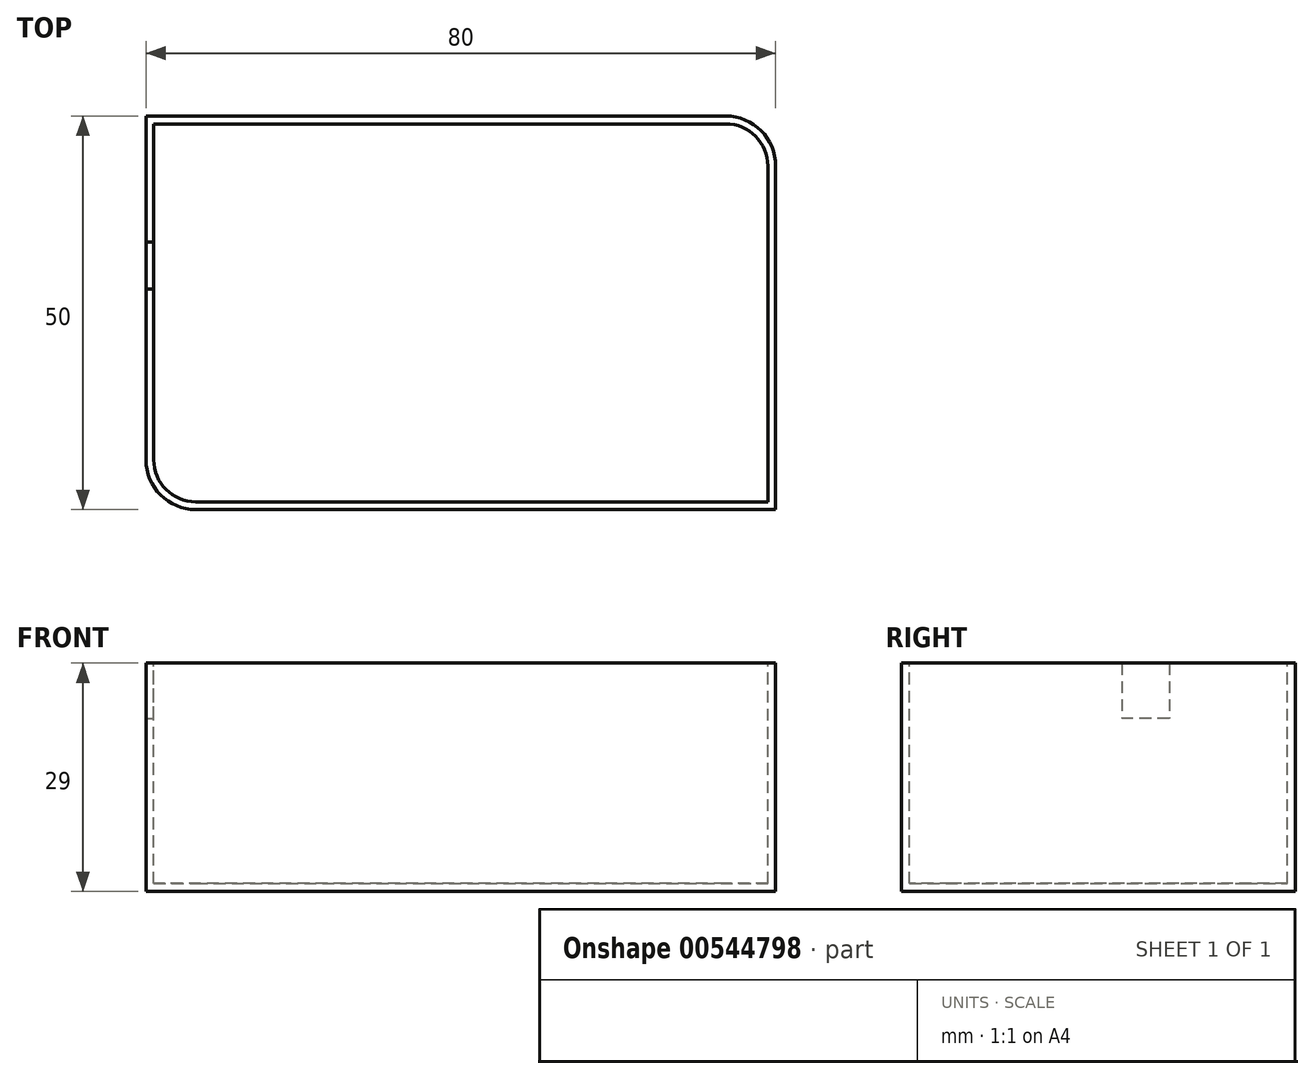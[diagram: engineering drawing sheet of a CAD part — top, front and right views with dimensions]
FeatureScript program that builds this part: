
annotation { "Feature Type Name" : "Feature", "Feature Type Description" : "" }
export const myFeature = defineFeature(function(context is Context, id is Id, definition is map)
    precondition{}
    {
        {
            var Q0;
            Q0=qCreatedBy(makeId("Top.planeOp"),FACE);
            var sketch = newSketch(context, id + "F0", { "sketchPlane" : qUnion([Q0])});
            skLineSegment(sketch, "E0.bottom", {"start": v(40, -25) * mm, "end": v(-33.65, -25) * mm});
            skLineSegment(sketch, "E0.top", {"start": v(33.65, 25) * mm, "end": v(-40, 25) * mm});
            skLineSegment(sketch, "E0.left", {"start": v(40, -25) * mm, "end": v(40, 18.65) * mm});
            skLineSegment(sketch, "E0.right", {"start": v(-40, -18.65) * mm, "end": v(-40, 25) * mm});
            skPoint(sketch, "E0.middle", {"position": v(0, 0) * mm});
            skPoint(sketch, "E1.visualSharp", {"position": v(-40, 25) * mm});
            skLineSegment(sketch, "E1.filletArc", {"start": v(-40, 25) * mm, "end": v(-40, 25) * mm});
            skPoint(sketch, "E2.visualSharp", {"position": v(40, -25) * mm});
            skLineSegment(sketch, "E2.filletArc", {"start": v(40, -25) * mm, "end": v(40, -25) * mm});
            skPoint(sketch, "E3.visualSharp", {"position": v(-40, -25) * mm});
            skArc(sketch, "E3.filletArc", {"start": v(-40, -18.65) * mm, "mid": v(-38.14, -23.14) * mm, "end": v(-33.65, -25) * mm});
            skPoint(sketch, "E4.visualSharp", {"position": v(40, 25) * mm});
            skArc(sketch, "E4.filletArc", {"start": v(40, 18.65) * mm, "mid": v(38.14, 23.14) * mm, "end": v(33.65, 25) * mm});
            skSolve(sketch);
        }
        {
            var Q0;
            Q0 = qSketchRegion(id + "F0", true);
            extrude(context, id + "F1", {"entities" : qUnion([Q0]), "depth" : 29 * mm, "offsetDistance" : 25.4 * mm});
        }
        {
            var Q0;
            Q0=makeQuery(id+"F1.opExtrude","CAP_FACE",FACE,{"disambiguationData":[OSD([sQuery(id+"F0.wireOp",EDGE,"E0.bottom"),sQuery(id+"F0.wireOp",EDGE,"E0.top"),sQuery(id+"F0.wireOp",EDGE,"E0.left"),sQuery(id+"F0.wireOp",EDGE,"E0.right"),sQuery(id+"F0.wireOp",EDGE,"E3.filletArc"),sQuery(id+"F0.wireOp",EDGE,"E4.filletArc")])],"isStart":false});
            var sketch = newSketch(context, id + "F2", { "sketchPlane" : qUnion([Q0])});
            skLineSegment(sketch, "E5.0", {"start": v(-39, 24) * mm, "end": v(-39, -18.67) * mm});
            skLineSegment(sketch, "E5.1", {"start": v(33.67, 24) * mm, "end": v(-39, 24) * mm});
            skLineSegment(sketch, "E5.2", {"start": v(39, -24) * mm, "end": v(39, 18.67) * mm});
            skLineSegment(sketch, "E5.3", {"start": v(-33.67, -24) * mm, "end": v(39, -24) * mm});
            skPoint(sketch, "E6.visualSharp", {"position": v(-39, -24) * mm});
            skArc(sketch, "E6.filletArc", {"start": v(-39, -18.67) * mm, "mid": v(-37.44, -22.44) * mm, "end": v(-33.67, -24) * mm});
            skPoint(sketch, "E7.visualSharp", {"position": v(39, 24) * mm});
            skArc(sketch, "E7.filletArc", {"start": v(39, 18.67) * mm, "mid": v(37.44, 22.44) * mm, "end": v(33.67, 24) * mm});
            skSolve(sketch);
        }
        {
            var Q0;
            Q0 = qSketchRegion(id + "F2", true);
            var Q1;
            Q1 = qSketchRegion(id + "F4", true);
            extrude(context, id + "F3", {"entities" : qUnion([Q0, Q1]), "operationType" : NewBodyOperationType.REMOVE, "oppositeDirection" : true, "depth" : 28 * mm, "offsetDistance" : 25.4 * mm});
        }
        {
            var Q0;
            Q0=makeQuery(id+"F3.boolean.opBoolean","COPY",FACE,{"derivedFrom":makeQuery(id+"F3.opExtrude","SWEPT_FACE",FACE,{"disambiguationData":[OSD([sQuery(id+"F2.wireOp",EDGE,"E5.0")])]})});
            var sketch = newSketch(context, id + "F4", { "sketchPlane" : qUnion([Q0])});
            skLineSegment(sketch, "E8.bottom", {"start": v(3, 22) * mm, "end": v(9, 22) * mm});
            skLineSegment(sketch, "E8.top", {"start": v(3, 29) * mm, "end": v(9, 29) * mm});
            skLineSegment(sketch, "E8.left", {"start": v(3, 22) * mm, "end": v(3, 29) * mm});
            skLineSegment(sketch, "E8.right", {"start": v(9, 22) * mm, "end": v(9, 29) * mm});
            skPoint(sketch, "E8.middle", {"position": v(6, 25.5) * mm});
            skSolve(sketch);
        }
        {
            var Q0;
            Q0 = qSketchRegion(id + "F4", true);
            extrude(context, id + "F5", {"entities" : qUnion([Q0]), "operationType" : NewBodyOperationType.REMOVE, "oppositeDirection" : true, "depth" : 44.45 * mm, "offsetDistance" : 25.4 * mm});
        }
    });
